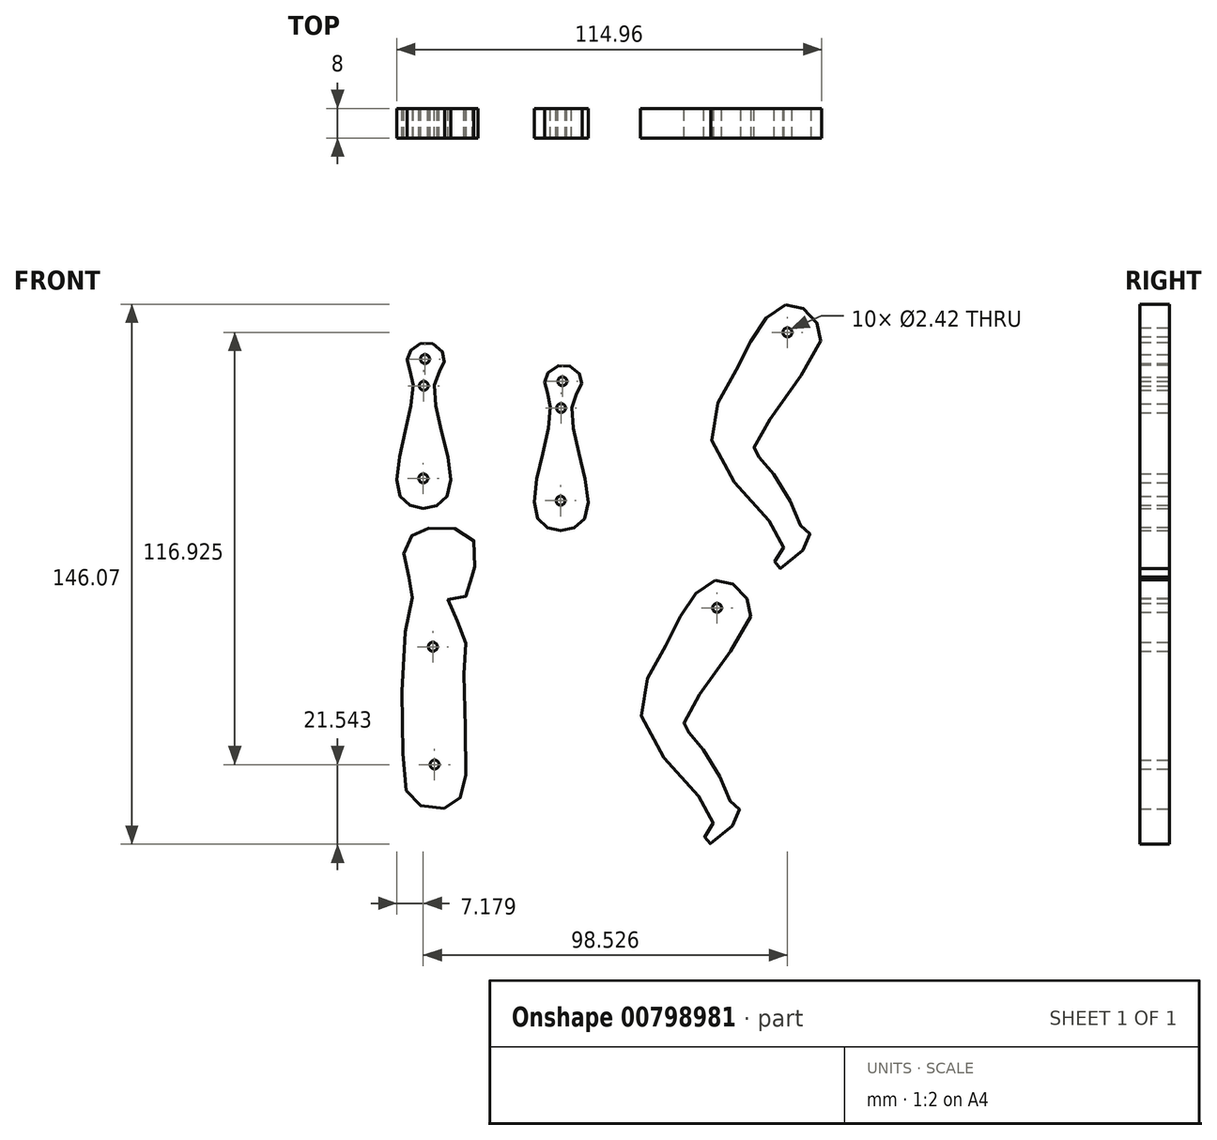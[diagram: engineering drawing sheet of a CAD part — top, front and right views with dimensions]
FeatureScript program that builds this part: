
annotation { "Feature Type Name" : "Feature", "Feature Type Description" : "" }
export const myFeature = defineFeature(function(context is Context, id is Id, definition is map)
    precondition{}
    {
        {
            var Q0;
            Q0=qCreatedBy(makeId("Front.planeOp"),FACE);
            var sketch = newSketch(context, id + "F0", { "sketchPlane" : qUnion([Q0])});
            skFitSpline(sketch, "E0", {"points": [v(-56.1, 51.3) * mm, v(-60.28, 23.14) * mm, v(-53.4, 17.92) * mm, v(-46.09, 23.14) * mm, v(-50.26, 51.3) * mm, v(-47.55, 58.6) * mm, v(-52.35, 62.78) * mm, v(-57.56, 59.03) * mm, v(-56.1, 51.3) * mm]});
            skFitSpline(sketch, "E1", {"points": [v(-58.24, -15.57) * mm, v(-58.51, -53.58) * mm, v(-56.75, -60.62) * mm, v(-51.48, -63.32) * mm, v(-45.93, -62.65) * mm, v(-43.1, -59.94) * mm, v(-41.74, -53.18) * mm, v(-42.28, -24.77) * mm, v(-42, -16.92) * mm, v(-45.4, -10.56) * mm, v(-46.34, -6.5) * mm, v(-42, -6.1) * mm, v(-40.66, -0.69) * mm, v(-38.63, -0.69) * mm, v(-39.98, 4.45) * mm, v(-39.98, 10.4) * mm, v(-47.7, 12.7) * mm, v(-53.5, 12.17) * mm, v(-56.62, 10.4) * mm, v(-58.51, 6.62) * mm, v(-57.57, 0) * mm, v(-56.21, -4.47) * mm, v(-58.24, -15.57) * mm]});
            skFitSpline(sketch, "E2", {"points": [v(25.63, -1.58) * mm, v(30.5, -2.66) * mm, v(34.56, -7.13) * mm, v(34.56, -13.08) * mm, v(17.38, -39.19) * mm, v(17.65, -41.49) * mm, v(18.87, -43.25) * mm, v(25.63, -52.04) * mm, v(30.1, -61.92) * mm, v(31.86, -63.27) * mm, v(32.53, -64.49) * mm, v(24.69, -72.74) * mm, v(22.66, -72.33) * mm, v(23.33, -70.03) * mm, v(25.1, -65.84) * mm, v(6.15, -40.27) * mm, v(11.83, -19.98) * mm, v(18.73, -7.13) * mm, v(25.63, -1.58) * mm]});
            skCircle(sketch, "E3", {"center": v(26.17, -9.02) * mm, "radius": 1.21 * mm});
            skCircle(sketch, "E4", {"center": v(-50.26, -51.42) * mm, "radius": 1.21 * mm});
            skCircle(sketch, "E5", {"center": v(-53.32, 26.01) * mm, "radius": 1.21 * mm});
            skCircle(sketch, "E6", {"center": v(-50.74, -19.55) * mm, "radius": 1.21 * mm});
            skCircle(sketch, "E7", {"center": v(-52.84, 58.3) * mm, "radius": 1.21 * mm});
            skCircle(sketch, "E8", {"center": v(-53.19, 51.07) * mm, "radius": 1.21 * mm});
            skFitSpline(sketch, "E9", {"points": [v(-18.95, 45.27) * mm, v(-23.12, 17.1) * mm, v(-16.24, 11.89) * mm, v(-8.93, 17.1) * mm, v(-13.1, 45.27) * mm, v(-10.4, 52.57) * mm, v(-15.2, 56.75) * mm, v(-20.4, 52.99) * mm, v(-18.95, 45.27) * mm]});
            skCircle(sketch, "E10", {"center": v(-16.17, 19.98) * mm, "radius": 1.21 * mm});
            skCircle(sketch, "E11", {"center": v(-15.69, 52.27) * mm, "radius": 1.21 * mm});
            skCircle(sketch, "E12", {"center": v(-16.03, 45.04) * mm, "radius": 1.21 * mm});
            skFitSpline(sketch, "E13", {"points": [v(44.66, 72.95) * mm, v(49.53, 71.87) * mm, v(53.6, 67.4) * mm, v(53.6, 61.45) * mm, v(36.41, 35.34) * mm, v(36.68, 33.04) * mm, v(37.9, 31.28) * mm, v(44.66, 22.49) * mm, v(49.13, 12.61) * mm, v(50.89, 11.26) * mm, v(51.56, 10.04) * mm, v(43.72, 1.8) * mm, v(41.69, 2.2) * mm, v(42.36, 4.5) * mm, v(44.12, 8.69) * mm, v(25.18, 34.26) * mm, v(30.87, 54.55) * mm, v(37.76, 67.4) * mm, v(44.66, 72.95) * mm]});
            skCircle(sketch, "E14", {"center": v(45.2, 65.5) * mm, "radius": 1.21 * mm});
            skSolve(sketch);
        }
        {
            var Q0;
            Q0 = qSketchRegion(id + "F0", true);
            extrude(context, id + "F1", {"entities" : qUnion([Q0]), "depth" : 8 * mm, "offsetDistance" : 25 * mm});
        }
    });
